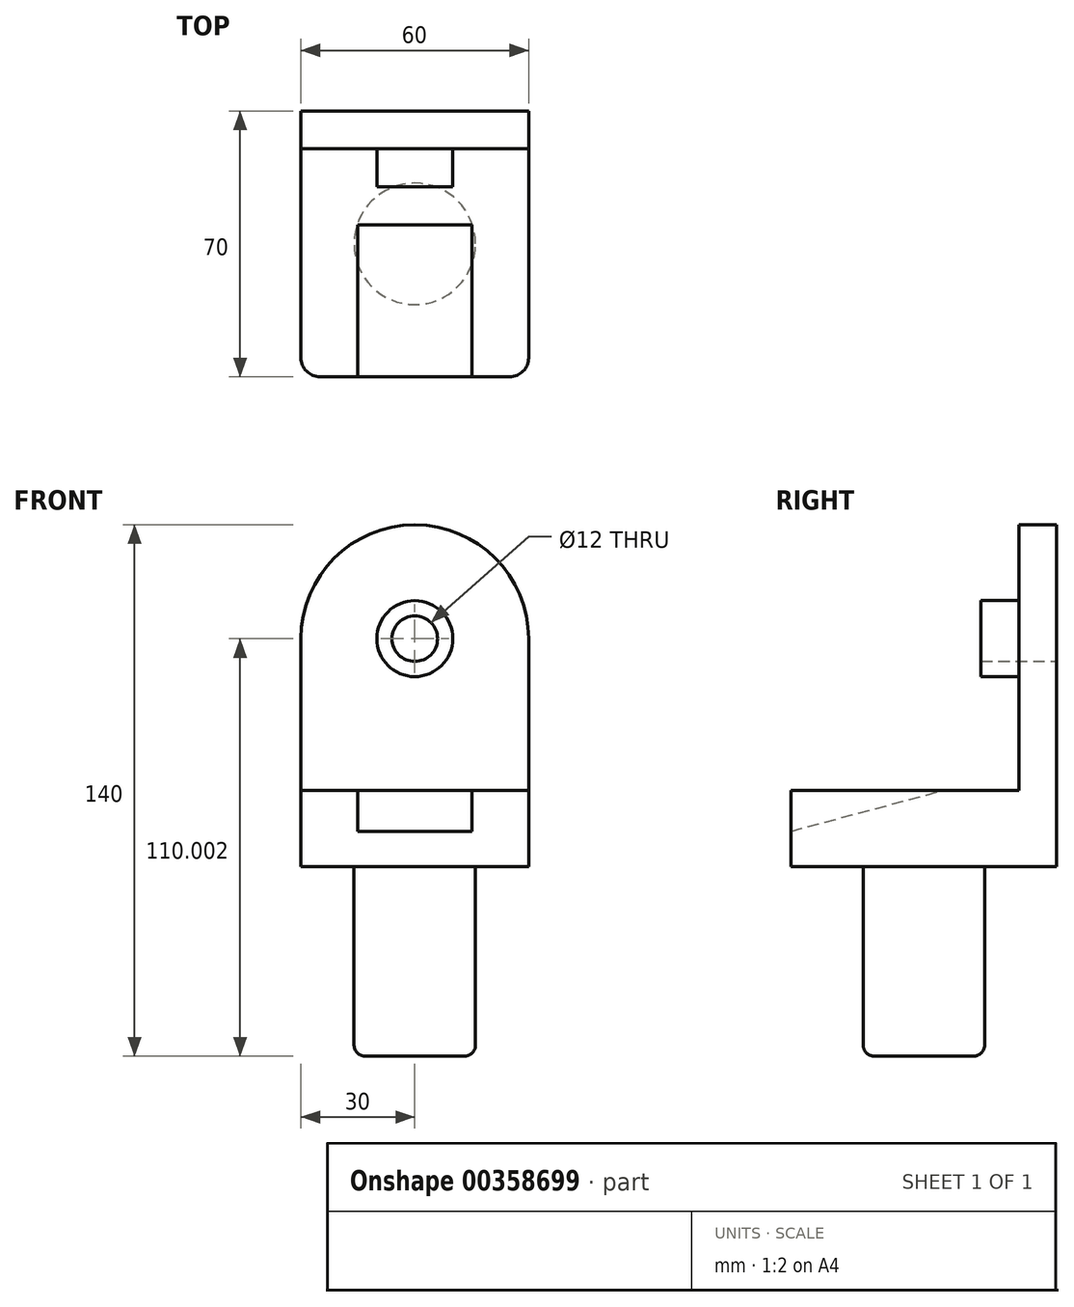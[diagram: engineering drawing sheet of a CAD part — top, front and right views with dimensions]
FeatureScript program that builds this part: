
annotation { "Feature Type Name" : "Feature", "Feature Type Description" : "" }
export const myFeature = defineFeature(function(context is Context, id is Id, definition is map)
    precondition{}
    {
        {
            var Q0;
            Q0=qCreatedBy(makeId("Front.planeOp"),FACE);
            var sketch = newSketch(context, id + "F0", { "sketchPlane" : qUnion([Q0])});
            skLineSegment(sketch, "E0", {"start": v(-60, -20.07) * mm, "end": v(0, -20.07) * mm});
            skLineSegment(sketch, "E1", {"start": v(0, -20.07) * mm, "end": v(0, -0.07) * mm});
            skLineSegment(sketch, "E2", {"start": v(0, -0.07) * mm, "end": v(-60, -0.07) * mm});
            skLineSegment(sketch, "E3", {"start": v(-60, -20.07) * mm, "end": v(-60, -0.07) * mm});
            skLineSegment(sketch, "E4", {"start": v(-60, -0.07) * mm, "end": v(-60, 39.93) * mm});
            skLineSegment(sketch, "E5", {"start": v(-30, 69.93) * mm, "end": v(-30, 69.93) * mm});
            skLineSegment(sketch, "E6", {"start": v(0, 39.93) * mm, "end": v(0, -0.07) * mm});
            skPoint(sketch, "E7.visualSharp", {"position": v(0, 69.93) * mm});
            skArc(sketch, "E7.filletArc", {"start": v(0, 39.93) * mm, "mid": v(-8.79, 61.15) * mm, "end": v(-30, 69.93) * mm});
            skPoint(sketch, "E8.visualSharp", {"position": v(-60, 69.93) * mm});
            skArc(sketch, "E8.filletArc", {"start": v(-30, 69.93) * mm, "mid": v(-51.21, 61.15) * mm, "end": v(-60, 39.93) * mm});
            skCircle(sketch, "E9", {"center": v(-30, 39.93) * mm, "radius": 6 * mm});
            skCircle(sketch, "E10", {"center": v(-30, 39.93) * mm, "radius": 10 * mm});
            skSolve(sketch);
        }
        {
            var Q0;
            Q0=makeQuery(id+"F0.imprint","IMPRINT",FACE,{"disambiguationData":[TD([[makeQuery(id+"F0.imprint","IMPRINT",EDGE,{"derivedFrom":sQuery(id+"F0.wireOp",EDGE,"E9")}),-1.0]])]});
            extrude(context, id + "F1", {"entities" : qUnion([Q0]), "depth" : 20 * mm});
        }
        {
            var Q0;
            Q0=makeQuery(id+"F0.imprint","IMPRINT",FACE,{"disambiguationData":[TD([[makeQuery(id+"F0.imprint","IMPRINT",EDGE,{"derivedFrom":sQuery(id+"F0.wireOp",EDGE,"E2")}),-1.0]])]});
            extrude(context, id + "F2", {"entities" : qUnion([Q0]), "operationType" : NewBodyOperationType.ADD, "depth" : 10 * mm});
        }
        {
            var Q0;
            Q0=makeQuery(id+"F0.imprint","IMPRINT",FACE,{"disambiguationData":[TD([[makeQuery(id+"F0.imprint","IMPRINT",EDGE,{"derivedFrom":sQuery(id+"F0.wireOp",EDGE,"E0")}),1.0]])]});
            extrude(context, id + "F3", {"entities" : qUnion([Q0]), "operationType" : NewBodyOperationType.ADD, "depth" : 70 * mm});
        }
        {
            var Q0;
            Q0=makeQuery(id+"F3.opExtrude","SWEPT_FACE",FACE,{"disambiguationData":[OSD([sQuery(id+"F0.wireOp",EDGE,"E0")])]});
            var sketch = newSketch(context, id + "F4", { "sketchPlane" : qUnion([Q0])});
            skPoint(sketch, "E11.startSnap0", {"position": v(-30, 0) * mm});
            skCircle(sketch, "E12", {"center": v(-30, 35) * mm, "radius": 16 * mm});
            skPoint(sketch, "E13.end.orphan", {"position": v(0, 35) * mm});
            skSolve(sketch);
        }
        {
            var Q0;
            Q0=makeQuery(id+"F4.imprint","IMPRINT",FACE,{"disambiguationData":[TD([[makeQuery(id+"F4.imprint","IMPRINT",EDGE,{"derivedFrom":sQuery(id+"F4.wireOp",EDGE,"E12")}),1.0]])]});
            extrude(context, id + "F5", {"entities" : qUnion([Q0]), "operationType" : NewBodyOperationType.ADD, "depth" : 50 * mm});
        }
        {
            var Q0;
            Q0=makeQuery(id+"F3.boolean.opBoolean","MERGE",FACE,{"derivedFrom":[makeQuery(id+"F2.opExtrude","SWEPT_FACE",FACE,{"disambiguationData":[OSD([sQuery(id+"F0.wireOp",EDGE,"E6")])]}),makeQuery(id+"F3.opExtrude","SWEPT_FACE",FACE,{"disambiguationData":[OSD([sQuery(id+"F0.wireOp",EDGE,"E1")])]})]});
            var sketch = newSketch(context, id + "F6", { "sketchPlane" : qUnion([Q0])});
            skLineSegment(sketch, "E14", {"start": v(-70, -0.07) * mm, "end": v(-30, -0.07) * mm});
            skLineSegment(sketch, "E15", {"start": v(-30, -0.07) * mm, "end": v(-70, -10.79) * mm});
            skLineSegment(sketch, "E16", {"start": v(-70, -10.79) * mm, "end": v(-70, -0.07) * mm});
            skSolve(sketch);
        }
        {
            var Q0;
            Q0=makeQuery(id+"F3.boolean.opBoolean","MERGE",FACE,{"derivedFrom":[makeQuery(id+"F2.opExtrude","SWEPT_FACE",FACE,{"disambiguationData":[OSD([sQuery(id+"F0.wireOp",EDGE,"E4")])]}),makeQuery(id+"F3.opExtrude","SWEPT_FACE",FACE,{"disambiguationData":[OSD([sQuery(id+"F0.wireOp",EDGE,"E3")])]})]});
            var sketch = newSketch(context, id + "F7", { "sketchPlane" : qUnion([Q0])});
            skLineSegment(sketch, "E17", {"start": v(70, -0.07) * mm, "end": v(30, -0.07) * mm});
            skLineSegment(sketch, "E18", {"start": v(30, -0.07) * mm, "end": v(70, -10.79) * mm});
            skLineSegment(sketch, "E19", {"start": v(70, -0.07) * mm, "end": v(70, -10.79) * mm});
            skSolve(sketch);
        }
        {
            var Q0;
            Q0=makeQuery(id+"F7.imprint","IMPRINT",FACE,{"disambiguationData":[TD([[makeQuery(id+"F7.imprint","IMPRINT",EDGE,{"derivedFrom":sQuery(id+"F7.wireOp",EDGE,"E17")}),1.0]])]});
            extrude(context, id + "F8", {"entities" : qUnion([Q0]), "operationType" : NewBodyOperationType.REMOVE, "oppositeDirection" : true, "depth" : 63.8 * mm});
        }
        {
            var Q0;
            Q0=makeQuery(id+"F6.imprint","IMPRINT",FACE,{"disambiguationData":[TD([[makeQuery(id+"F6.imprint","IMPRINT",EDGE,{"derivedFrom":sQuery(id+"F6.wireOp",EDGE,"E14")}),-1.0]])]});
            var Q1;
            {var subQ4=sQuery(id+"F6.wireOp",EDGE,"E15");Q1=makeQuery(id+"F6.imprint","IMPRINT",FACE,{"disambiguationData":[TD([[makeQuery(id+"F6.imprint","IMPRINT",EDGE,{"derivedFrom":subQ4}),1.0]])]});}
            extrude(context, id + "F9", {"entities" : qUnion([Q0, Q1]), "operationType" : NewBodyOperationType.ADD, "oppositeDirection" : true, "depth" : 15 * mm});
        }
        {
            var Q0;
            Q0=makeQuery(id+"F7.imprint","IMPRINT",FACE,{"disambiguationData":[TD([[makeQuery(id+"F7.imprint","IMPRINT",EDGE,{"derivedFrom":sQuery(id+"F7.wireOp",EDGE,"E17")}),1.0]])]});
            var Q1;
            {var subQ4=sQuery(id+"F7.wireOp",EDGE,"E18");Q1=makeQuery(id+"F7.imprint","IMPRINT",FACE,{"disambiguationData":[TD([[makeQuery(id+"F7.imprint","IMPRINT",EDGE,{"derivedFrom":subQ4}),-1.0]])]});}
            extrude(context, id + "F10", {"entities" : qUnion([Q0, Q1]), "operationType" : NewBodyOperationType.ADD, "oppositeDirection" : true, "depth" : 15 * mm});
        }
        {
            var Q0;
            Q0=makeQuery(id+"F5.opExtrude","CAP_EDGE",EDGE,{"disambiguationData":[OSD([sQuery(id+"F4.wireOp",EDGE,"E12")])],"isStart":false});
            fillet(context, id + "F11", {"entities" : qUnion([Q0]), "radius" : 3 * mm, "tangentPropagation" : true, "allowEdgeOverflow" : false});
        }
        {
            var Q0;
            {var subQ0=sQuery(id+"F0.wireOp",EDGE,"E3");Q0=makeQuery(id+"F10.boolean.opBoolean","MERGE",EDGE,{"derivedFrom":[makeQuery(id+"F3.opExtrude","CAP_EDGE",EDGE,{"disambiguationData":[OSD([subQ0])],"isStart":false}),makeQuery(id+"F10.opExtrude","CAP_EDGE",EDGE,{"disambiguationData":[OSD([subQ0,sQuery(id+"F7.wireOp",EDGE,"E19")])],"isStart":true})]});}
            var Q1;
            {var subQ0=sQuery(id+"F0.wireOp",EDGE,"E1");Q1=makeQuery(id+"F9.boolean.opBoolean","MERGE",EDGE,{"derivedFrom":[makeQuery(id+"F3.opExtrude","CAP_EDGE",EDGE,{"disambiguationData":[OSD([subQ0])],"isStart":false}),makeQuery(id+"F9.opExtrude","CAP_EDGE",EDGE,{"disambiguationData":[OSD([subQ0,sQuery(id+"F6.wireOp",EDGE,"E16")])],"isStart":true})]});}
            fillet(context, id + "F12", {"entities" : qUnion([Q0, Q1]), "radius" : 5 * mm, "tangentPropagation" : true, "allowEdgeOverflow" : false});
        }
    });
